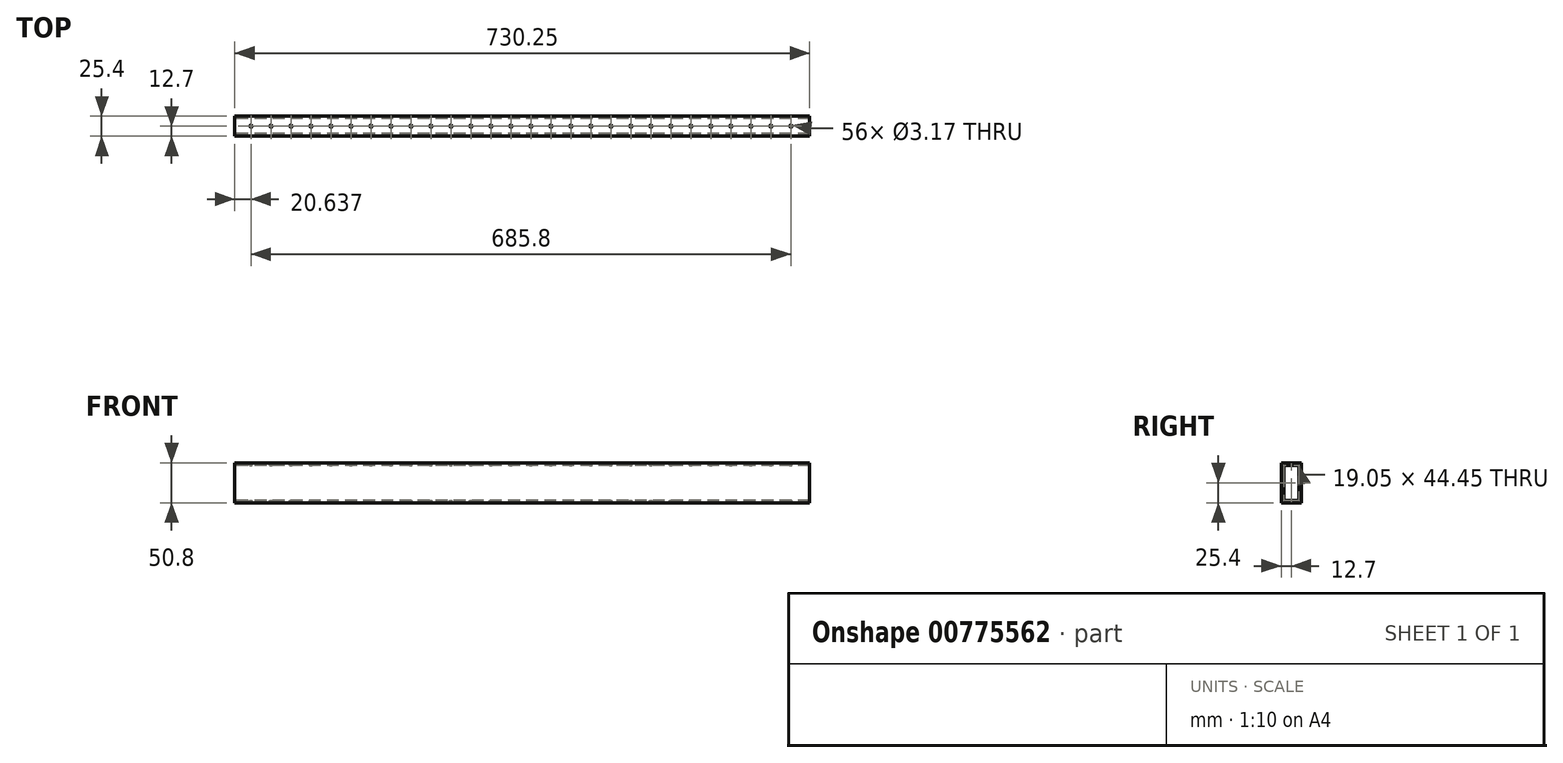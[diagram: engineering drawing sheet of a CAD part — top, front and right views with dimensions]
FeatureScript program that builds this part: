
annotation { "Feature Type Name" : "Feature", "Feature Type Description" : "" }
export const myFeature = defineFeature(function(context is Context, id is Id, definition is map)
    precondition{}
    {
        {
            var Q0;
            Q0=qCreatedBy(makeId("Right.planeOp"),FACE);
            var sketch = newSketch(context, id + "F0", { "sketchPlane" : qUnion([Q0])});
            skLineSegment(sketch, "E0.bottom", {"start": v(12.7, 25.4) * mm, "end": v(-12.7, 25.4) * mm});
            skLineSegment(sketch, "E0.top", {"start": v(12.7, -25.4) * mm, "end": v(-12.7, -25.4) * mm});
            skLineSegment(sketch, "E0.left", {"start": v(12.7, 25.4) * mm, "end": v(12.7, -25.4) * mm});
            skLineSegment(sketch, "E0.right", {"start": v(-12.7, 25.4) * mm, "end": v(-12.7, -25.4) * mm});
            skPoint(sketch, "E0.middle", {"position": v(0, 0) * mm});
            skLineSegment(sketch, "E1.bottom", {"start": v(9.52, 22.23) * mm, "end": v(-9.53, 22.23) * mm});
            skLineSegment(sketch, "E1.top", {"start": v(9.53, -22.23) * mm, "end": v(-9.52, -22.23) * mm});
            skLineSegment(sketch, "E1.left", {"start": v(9.52, 22.23) * mm, "end": v(9.53, -22.22) * mm});
            skLineSegment(sketch, "E1.right", {"start": v(-9.53, 22.22) * mm, "end": v(-9.52, -22.23) * mm});
            skSolve(sketch);
        }
        {
            var Q0;
            Q0 = qSketchRegion(id + "F0", true);
            extrude(context, id + "F1", {"entities" : qUnion([Q0]), "depth" : 730.25 * mm, "offsetDistance" : 25.4 * mm});
        }
        {
            var Q0;
            Q0=makeQuery(id+"F1.opExtrude","SWEPT_FACE",FACE,{"disambiguationData":[OSD([sQuery(id+"F0.wireOp",EDGE,"E0.bottom")])]});
            var sketch = newSketch(context, id + "F2", { "sketchPlane" : qUnion([Q0])});
            skCircle(sketch, "E2", {"center": v(20.64, 0) * mm, "radius": 1.59 * mm});
            skCircle(sketch, "E3.1.0.0", {"center": v(46.04, 0) * mm, "radius": 1.59 * mm});
            skCircle(sketch, "E3.2.0.0", {"center": v(71.44, 0) * mm, "radius": 1.59 * mm});
            skCircle(sketch, "E3.3.0.0", {"center": v(96.84, 0) * mm, "radius": 1.59 * mm});
            skCircle(sketch, "E3.4.0.0", {"center": v(122.24, 0) * mm, "radius": 1.59 * mm});
            skCircle(sketch, "E3.5.0.0", {"center": v(147.64, 0) * mm, "radius": 1.59 * mm});
            skCircle(sketch, "E3.6.0.0", {"center": v(173.04, 0) * mm, "radius": 1.59 * mm});
            skCircle(sketch, "E3.7.0.0", {"center": v(198.44, 0) * mm, "radius": 1.59 * mm});
            skCircle(sketch, "E3.8.0.0", {"center": v(223.84, 0) * mm, "radius": 1.59 * mm});
            skCircle(sketch, "E3.9.0.0", {"center": v(249.24, 0) * mm, "radius": 1.59 * mm});
            skCircle(sketch, "E3.10.0.0", {"center": v(274.64, 0) * mm, "radius": 1.59 * mm});
            skCircle(sketch, "E3.11.0.0", {"center": v(300.04, 0) * mm, "radius": 1.59 * mm});
            skCircle(sketch, "E3.12.0.0", {"center": v(325.44, 0) * mm, "radius": 1.59 * mm});
            skCircle(sketch, "E3.13.0.0", {"center": v(350.84, 0) * mm, "radius": 1.59 * mm});
            skCircle(sketch, "E3.14.0.0", {"center": v(376.24, 0) * mm, "radius": 1.59 * mm});
            skCircle(sketch, "E3.15.0.0", {"center": v(401.64, 0) * mm, "radius": 1.59 * mm});
            skCircle(sketch, "E3.16.0.0", {"center": v(427.04, 0) * mm, "radius": 1.59 * mm});
            skCircle(sketch, "E3.17.0.0", {"center": v(452.44, 0) * mm, "radius": 1.59 * mm});
            skCircle(sketch, "E3.18.0.0", {"center": v(477.84, 0) * mm, "radius": 1.59 * mm});
            skCircle(sketch, "E3.19.0.0", {"center": v(503.24, 0) * mm, "radius": 1.59 * mm});
            skCircle(sketch, "E3.20.0.0", {"center": v(528.64, 0) * mm, "radius": 1.59 * mm});
            skCircle(sketch, "E3.21.0.0", {"center": v(554.04, 0) * mm, "radius": 1.59 * mm});
            skCircle(sketch, "E3.22.0.0", {"center": v(579.44, 0) * mm, "radius": 1.59 * mm});
            skCircle(sketch, "E3.23.0.0", {"center": v(604.84, 0) * mm, "radius": 1.59 * mm});
            skCircle(sketch, "E3.24.0.0", {"center": v(630.24, 0) * mm, "radius": 1.59 * mm});
            skCircle(sketch, "E3.25.0.0", {"center": v(655.64, 0) * mm, "radius": 1.59 * mm});
            skCircle(sketch, "E3.26.0.0", {"center": v(681.04, 0) * mm, "radius": 1.59 * mm});
            skCircle(sketch, "E3.27.0.0", {"center": v(706.44, 0) * mm, "radius": 1.59 * mm});
            skCircle(sketch, "E3.28.0.0", {"center": v(731.84, 0) * mm, "radius": 1.59 * mm});
            skLineSegment(sketch, "E3.direction1", {"start": v(20.64, 0) * mm, "end": v(46.04, 0) * mm, "construction": true});
            skCircle(sketch, "E4.0.29.0", {"center": v(757.24, 0) * mm, "radius": 1.59 * mm});
            skSolve(sketch);
        }
        {
            var Q0;
            Q0 = qSketchRegion(id + "F2", true);
            extrude(context, id + "F3", {"entities" : qUnion([Q0]), "operationType" : NewBodyOperationType.REMOVE, "endBound" : BoundingType.THROUGH_ALL, "oppositeDirection" : true, "depth" : 25.4 * mm, "offsetDistance" : 25.4 * mm});
        }
    });
